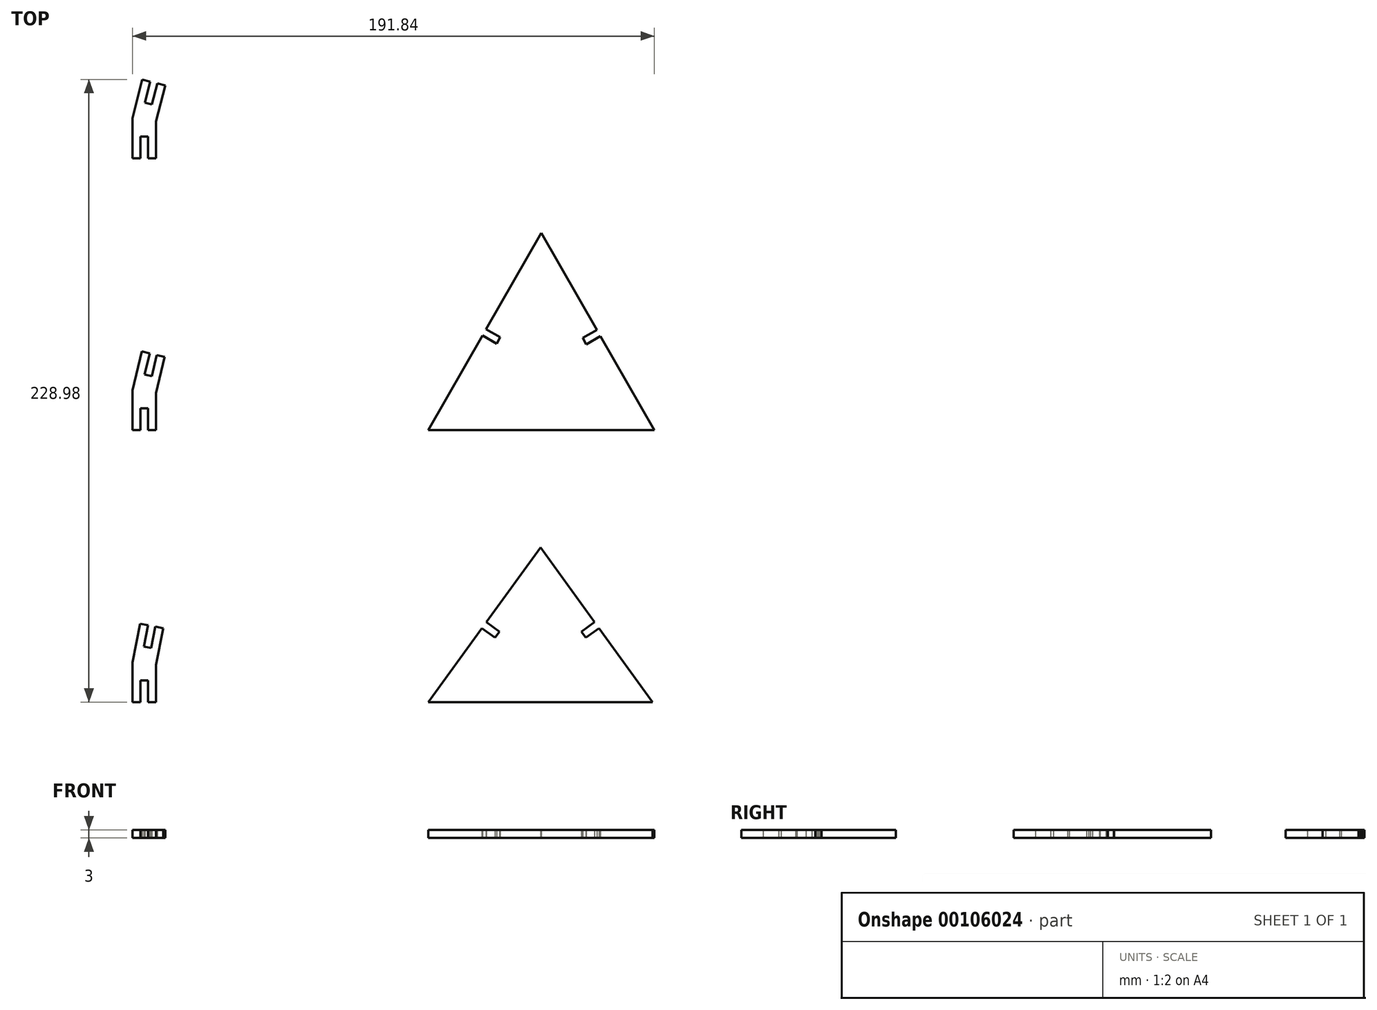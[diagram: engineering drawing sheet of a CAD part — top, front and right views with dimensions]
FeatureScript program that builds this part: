
annotation { "Feature Type Name" : "Feature", "Feature Type Description" : "" }
export const myFeature = defineFeature(function(context is Context, id is Id, definition is map)
    precondition{}
    {
        {
            assignVariable(context, id + "F0", {"name" : "sheet_height", "anyValue" : 3});
        }
        {
            var Q0;
            Q0=qCreatedBy(makeId("Top.planeOp"),FACE);
            var sketch = newSketch(context, id + "F1", { "sketchPlane" : qUnion([Q0])});
            skLineSegment(sketch, "E0", {"start": v(0, 0) * mm, "end": v(83.14, 0) * mm});
            skLineSegment(sketch, "E1", {"start": v(83.14, 0) * mm, "end": v(41.57, 72.5) * mm});
            skLineSegment(sketch, "E2", {"start": v(41.57, 72.5) * mm, "end": v(0, 0) * mm});
            skLineSegment(sketch, "E3", {"start": v(41.57, 72.5) * mm, "end": v(41.57, 0) * mm, "construction": true});
            skLineSegment(sketch, "E4", {"start": v(83.14, 0) * mm, "end": v(20.56, 35.87) * mm, "construction": true});
            skLineSegment(sketch, "E5", {"start": v(0, 0) * mm, "end": v(62.57, 35.87) * mm, "construction": true});
            skLineSegment(sketch, "E6", {"start": v(21.31, 37.17) * mm, "end": v(26.52, 34.19) * mm});
            skLineSegment(sketch, "E7", {"start": v(26.52, 34.19) * mm, "end": v(25.17, 31.85) * mm});
            skLineSegment(sketch, "E8", {"start": v(25.17, 31.85) * mm, "end": v(19.97, 34.83) * mm});
            skLineSegment(sketch, "E9", {"start": v(61.98, 36.91) * mm, "end": v(56.77, 33.93) * mm});
            skLineSegment(sketch, "E10", {"start": v(56.77, 33.93) * mm, "end": v(58.11, 31.59) * mm});
            skLineSegment(sketch, "E11", {"start": v(58.11, 31.59) * mm, "end": v(63.32, 34.57) * mm});
            skSolve(sketch);
        }
        {
            var Q0;
            {var subQ7=sQuery(id+"F1.wireOp",EDGE,"E6");Q0=makeQuery(id+"F1.imprint","IMPRINT",FACE,{"disambiguationData":[TD([[makeQuery(id+"F1.imprint","IMPRINT",EDGE,{"derivedFrom":subQ7}),1.0]])]});}
            extrude(context, id + "F2", {"entities" : qUnion([Q0]), "depth" : (getVariable(context, 'sheet_height')) * mm});
        }
        {
            var Q0;
            Q0=qCreatedBy(makeId("Top.planeOp"),FACE);
            var sketch = newSketch(context, id + "F3", { "sketchPlane" : qUnion([Q0])});
            skLineSegment(sketch, "E12", {"start": v(0, 0) * mm, "end": v(0, -100) * mm, "construction": true});
            skLineSegment(sketch, "E13", {"start": v(0, -100) * mm, "end": v(82.54, -100) * mm});
            skLineSegment(sketch, "E14", {"start": v(82.54, -100) * mm, "end": v(41.27, -43.2) * mm});
            skLineSegment(sketch, "E15", {"start": v(41.27, -43.2) * mm, "end": v(0, -100) * mm});
            skLineSegment(sketch, "E16", {"start": v(41.27, -43.2) * mm, "end": v(41.27, -100) * mm, "construction": true});
            skLineSegment(sketch, "E17", {"start": v(0, -100) * mm, "end": v(54.02, -60.75) * mm, "construction": true});
            skLineSegment(sketch, "E18", {"start": v(82.54, -100) * mm, "end": v(28.52, -60.75) * mm, "construction": true});
            skLineSegment(sketch, "E19", {"start": v(19.75, -72.81) * mm, "end": v(24.6, -76.34) * mm});
            skLineSegment(sketch, "E20", {"start": v(24.6, -76.34) * mm, "end": v(26.2, -74.16) * mm});
            skLineSegment(sketch, "E21", {"start": v(26.2, -74.16) * mm, "end": v(21.34, -70.63) * mm});
            skLineSegment(sketch, "E22", {"start": v(61.2, -70.63) * mm, "end": v(56.34, -74.16) * mm});
            skLineSegment(sketch, "E23", {"start": v(56.34, -74.16) * mm, "end": v(57.93, -76.34) * mm});
            skLineSegment(sketch, "E24", {"start": v(57.93, -76.34) * mm, "end": v(62.78, -72.81) * mm});
            skPoint(sketch, "E25", {"position": v(20.63, -71.6) * mm});
            skPoint(sketch, "E26", {"position": v(61.9, -71.6) * mm});
            skSolve(sketch);
        }
        {
            var Q0;
            {var subQ4=sQuery(id+"F3.wireOp",EDGE,"E19");Q0=makeQuery(id+"F3.imprint","IMPRINT",FACE,{"disambiguationData":[TD([[makeQuery(id+"F3.imprint","IMPRINT",EDGE,{"derivedFrom":subQ4}),-1.0]])]});}
            extrude(context, id + "F4", {"entities" : qUnion([Q0]), "depth" : (getVariable(context, 'sheet_height')) * mm});
        }
        {
            var Q0;
            Q0=qCreatedBy(makeId("Top.planeOp"),FACE);
            var sketch = newSketch(context, id + "F5", { "sketchPlane" : qUnion([Q0])});
            skLineSegment(sketch, "E27", {"start": v(0, 0) * mm, "end": v(-100, 0) * mm, "construction": true});
            skLineSegment(sketch, "E28", {"start": v(-100, 0) * mm, "end": v(-100, 13.64) * mm});
            skLineSegment(sketch, "E29", {"start": v(-103, 0) * mm, "end": v(-100, 0) * mm});
            skLineSegment(sketch, "E30", {"start": v(-103, 0) * mm, "end": v(-103, 8) * mm});
            skLineSegment(sketch, "E31", {"start": v(-103, 8) * mm, "end": v(-105.7, 8) * mm});
            skLineSegment(sketch, "E32", {"start": v(-105.7, 8) * mm, "end": v(-105.7, 0) * mm});
            skLineSegment(sketch, "E33", {"start": v(-105.7, 0) * mm, "end": v(-108.7, 0) * mm});
            skLineSegment(sketch, "E34", {"start": v(-108.7, 0) * mm, "end": v(-108.7, 14.68) * mm});
            skLineSegment(sketch, "E35", {"start": v(-108.7, 14.68) * mm, "end": v(-105.25, 28.95) * mm});
            skLineSegment(sketch, "E36", {"start": v(-105.25, 28.95) * mm, "end": v(-102.33, 28.24) * mm});
            skLineSegment(sketch, "E37", {"start": v(-102.33, 28.24) * mm, "end": v(-104.21, 20.47) * mm});
            skLineSegment(sketch, "E38", {"start": v(-104.21, 20.47) * mm, "end": v(-101.59, 19.83) * mm});
            skLineSegment(sketch, "E39", {"start": v(-101.59, 19.83) * mm, "end": v(-99.7, 27.6) * mm});
            skLineSegment(sketch, "E40", {"start": v(-99.7, 27.6) * mm, "end": v(-96.8, 26.9) * mm});
            skLineSegment(sketch, "E41", {"start": v(-96.8, 26.9) * mm, "end": v(-100, 13.64) * mm});
            skLineSegment(sketch, "E42", {"start": v(-108.7, 14.68) * mm, "end": v(-100, 13.64) * mm, "construction": true});
            skLineSegment(sketch, "E43", {"start": v(-101.59, 19.83) * mm, "end": v(-103, 14) * mm, "construction": true});
            skSolve(sketch);
        }
        {
            var Q0;
            Q0=makeQuery(id+"F5.imprint","IMPRINT",FACE,{"disambiguationData":[TD([[makeQuery(id+"F5.imprint","IMPRINT",EDGE,{"derivedFrom":sQuery(id+"F5.wireOp",EDGE,"E28")}),1.0]])]});
            extrude(context, id + "F6", {"entities" : qUnion([Q0]), "depth" : (getVariable(context, 'sheet_height')) * mm});
        }
        {
            var Q0;
            Q0=qCreatedBy(makeId("Top.planeOp"),FACE);
            var sketch = newSketch(context, id + "F7", { "sketchPlane" : qUnion([Q0])});
            skLineSegment(sketch, "E44", {"start": v(0, -100) * mm, "end": v(-100, -100) * mm, "construction": true});
            skLineSegment(sketch, "E45", {"start": v(-100, -100) * mm, "end": v(-100, -86.3) * mm});
            skLineSegment(sketch, "E46", {"start": v(-103, -100) * mm, "end": v(-100, -100) * mm});
            skLineSegment(sketch, "E47", {"start": v(-103, -100) * mm, "end": v(-103, -92) * mm});
            skLineSegment(sketch, "E48", {"start": v(-103, -92) * mm, "end": v(-105.7, -92) * mm});
            skLineSegment(sketch, "E49", {"start": v(-105.7, -92) * mm, "end": v(-105.7, -100) * mm});
            skLineSegment(sketch, "E50", {"start": v(-105.7, -100) * mm, "end": v(-108.7, -100) * mm});
            skLineSegment(sketch, "E51", {"start": v(-108.7, -100) * mm, "end": v(-108.7, -85.44) * mm});
            skLineSegment(sketch, "E52", {"start": v(-108.7, -85.44) * mm, "end": v(-105.85, -71.15) * mm});
            skLineSegment(sketch, "E53", {"start": v(-105.85, -71.15) * mm, "end": v(-102.9, -71.74) * mm});
            skLineSegment(sketch, "E54", {"start": v(-102.9, -71.74) * mm, "end": v(-104.47, -79.59) * mm});
            skLineSegment(sketch, "E55", {"start": v(-104.47, -79.59) * mm, "end": v(-101.82, -80.12) * mm});
            skLineSegment(sketch, "E56", {"start": v(-101.82, -80.12) * mm, "end": v(-100.26, -72.27) * mm});
            skLineSegment(sketch, "E57", {"start": v(-100.26, -72.27) * mm, "end": v(-97.31, -72.86) * mm});
            skLineSegment(sketch, "E58", {"start": v(-97.31, -72.86) * mm, "end": v(-100, -86.3) * mm});
            skLineSegment(sketch, "E59", {"start": v(-108.7, -85.44) * mm, "end": v(-100, -86.3) * mm, "construction": true});
            skLineSegment(sketch, "E60", {"start": v(-101.82, -80.12) * mm, "end": v(-103, -86) * mm, "construction": true});
            skSolve(sketch);
        }
        {
            var Q0;
            Q0=makeQuery(id+"F7.imprint","IMPRINT",FACE,{"disambiguationData":[TD([[makeQuery(id+"F7.imprint","IMPRINT",EDGE,{"derivedFrom":sQuery(id+"F7.wireOp",EDGE,"E45")}),1.0]])]});
            extrude(context, id + "F8", {"entities" : qUnion([Q0]), "depth" : (getVariable(context, 'sheet_height')) * mm});
        }
        {
            var Q0;
            Q0=qCreatedBy(makeId("Top.planeOp"),FACE);
            var sketch = newSketch(context, id + "F9", { "sketchPlane" : qUnion([Q0])});
            skLineSegment(sketch, "E61", {"start": v(0, 100) * mm, "end": v(-100, 100) * mm, "construction": true});
            skLineSegment(sketch, "E62", {"start": v(-100, 100) * mm, "end": v(-100, 113.62) * mm});
            skLineSegment(sketch, "E63", {"start": v(-103, 100) * mm, "end": v(-100, 100) * mm});
            skLineSegment(sketch, "E64", {"start": v(-103, 100) * mm, "end": v(-103, 108) * mm});
            skLineSegment(sketch, "E65", {"start": v(-103, 108) * mm, "end": v(-105.7, 108) * mm});
            skLineSegment(sketch, "E66", {"start": v(-105.7, 108) * mm, "end": v(-105.7, 100) * mm});
            skLineSegment(sketch, "E67", {"start": v(-105.7, 100) * mm, "end": v(-108.7, 100) * mm});
            skLineSegment(sketch, "E68", {"start": v(-108.7, 100) * mm, "end": v(-108.7, 114.72) * mm});
            skLineSegment(sketch, "E69", {"start": v(-108.7, 114.72) * mm, "end": v(-105.04, 128.98) * mm});
            skLineSegment(sketch, "E70", {"start": v(-105.04, 128.98) * mm, "end": v(-102.13, 128.23) * mm});
            skLineSegment(sketch, "E71", {"start": v(-102.13, 128.23) * mm, "end": v(-104.12, 120.48) * mm});
            skLineSegment(sketch, "E72", {"start": v(-104.12, 120.48) * mm, "end": v(-101.5, 119.81) * mm});
            skLineSegment(sketch, "E73", {"start": v(-101.5, 119.81) * mm, "end": v(-99.52, 127.56) * mm});
            skLineSegment(sketch, "E74", {"start": v(-99.52, 127.56) * mm, "end": v(-96.61, 126.81) * mm});
            skLineSegment(sketch, "E75", {"start": v(-96.61, 126.81) * mm, "end": v(-100, 113.62) * mm});
            skLineSegment(sketch, "E76", {"start": v(-108.7, 114.72) * mm, "end": v(-100, 113.62) * mm, "construction": true});
            skLineSegment(sketch, "E77", {"start": v(-101.5, 119.81) * mm, "end": v(-103, 114) * mm, "construction": true});
            skLineSegment(sketch, "E78", {"start": v(0, 0) * mm, "end": v(0, 100) * mm, "construction": true});
            skSolve(sketch);
        }
        {
            var Q0;
            Q0=makeQuery(id+"F9.imprint","IMPRINT",FACE,{"disambiguationData":[TD([[makeQuery(id+"F9.imprint","IMPRINT",EDGE,{"derivedFrom":sQuery(id+"F9.wireOp",EDGE,"E62")}),1.0]])]});
            extrude(context, id + "F10", {"entities" : qUnion([Q0]), "depth" : (getVariable(context, 'sheet_height')) * mm});
        }
    });
